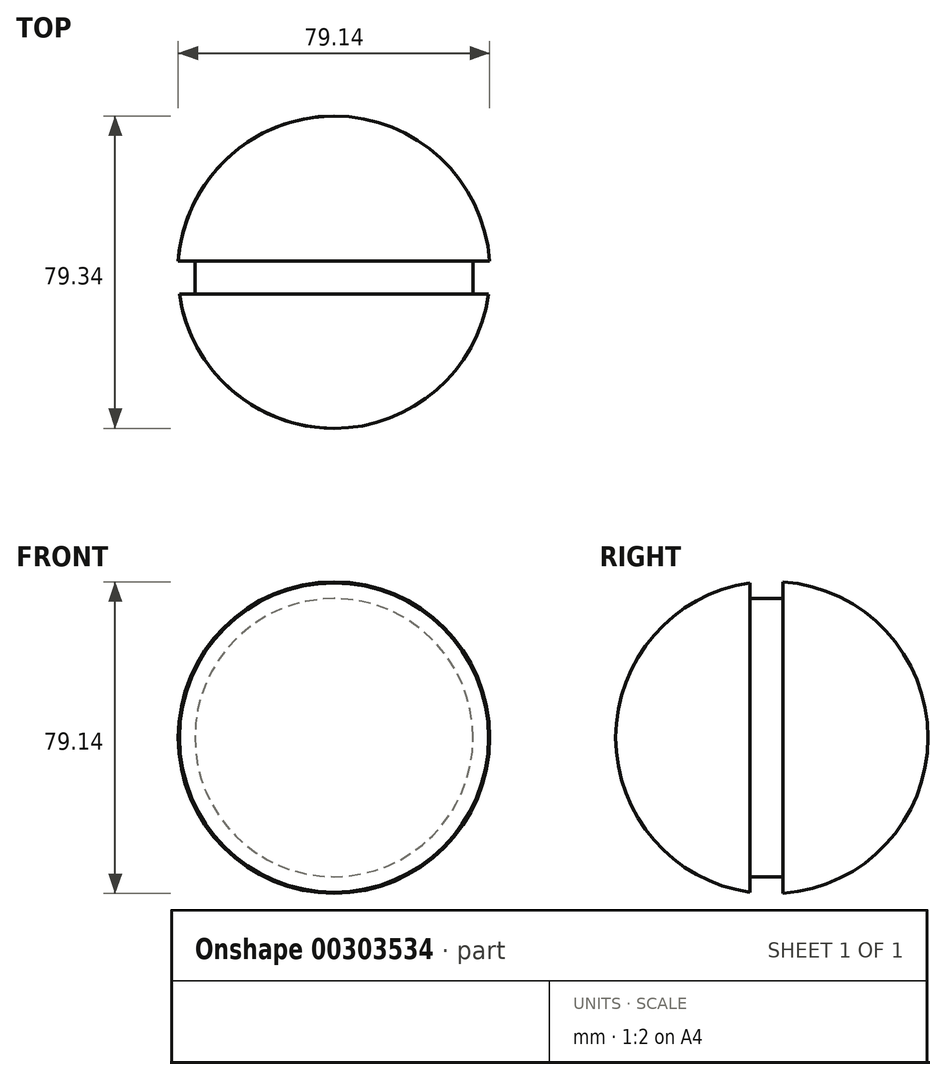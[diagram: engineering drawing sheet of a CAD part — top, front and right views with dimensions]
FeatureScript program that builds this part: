
annotation { "Feature Type Name" : "Feature", "Feature Type Description" : "" }
export const myFeature = defineFeature(function(context is Context, id is Id, definition is map)
    precondition{}
    {
        {
            var Q0;
            Q0=qCreatedBy(makeId("Top.planeOp"),FACE);
            var sketch = newSketch(context, id + "F0", { "sketchPlane" : qUnion([Q0])});
            skArc(sketch, "E0", {"start": v(0, 75.15) * mm, "mid": v(-27.05, 64.5) * mm, "end": v(-39.57, 38.28) * mm});
            skLineSegment(sketch, "E1", {"start": v(0, -4.19) * mm, "end": v(0, 75.15) * mm});
            skLineSegment(sketch, "E2", {"start": v(-39.57, 38.28) * mm, "end": v(-35.32, 38.28) * mm});
            skLineSegment(sketch, "E3", {"start": v(-39.28, 29.92) * mm, "end": v(-35.32, 29.92) * mm});
            skArc(sketch, "E4.trimOffspring", {"start": v(-39.28, 29.92) * mm, "mid": v(-26.01, 5.53) * mm, "end": v(0, -4.19) * mm});
            skLineSegment(sketch, "E5", {"start": v(-35.32, 29.92) * mm, "end": v(-35.32, 38.28) * mm});
            skPoint(sketch, "E6.orphan", {"position": v(-22.61, 29.92) * mm});
            skPoint(sketch, "E7.orphan", {"position": v(-22.61, 38.28) * mm});
            skSolve(sketch);
        }
        {
            var Q0;
            Q0 = qSketchRegion(id + "F0", true);
            var Q1;
            Q1=sQuery(id+"F0.wireOp",EDGE,"E1");
            revolve(context, id + "F1", {"entities" : qUnion([Q0]), "axis" : qUnion([Q1]), "revolveType" : RevolveType.FULL});
        }
    });
